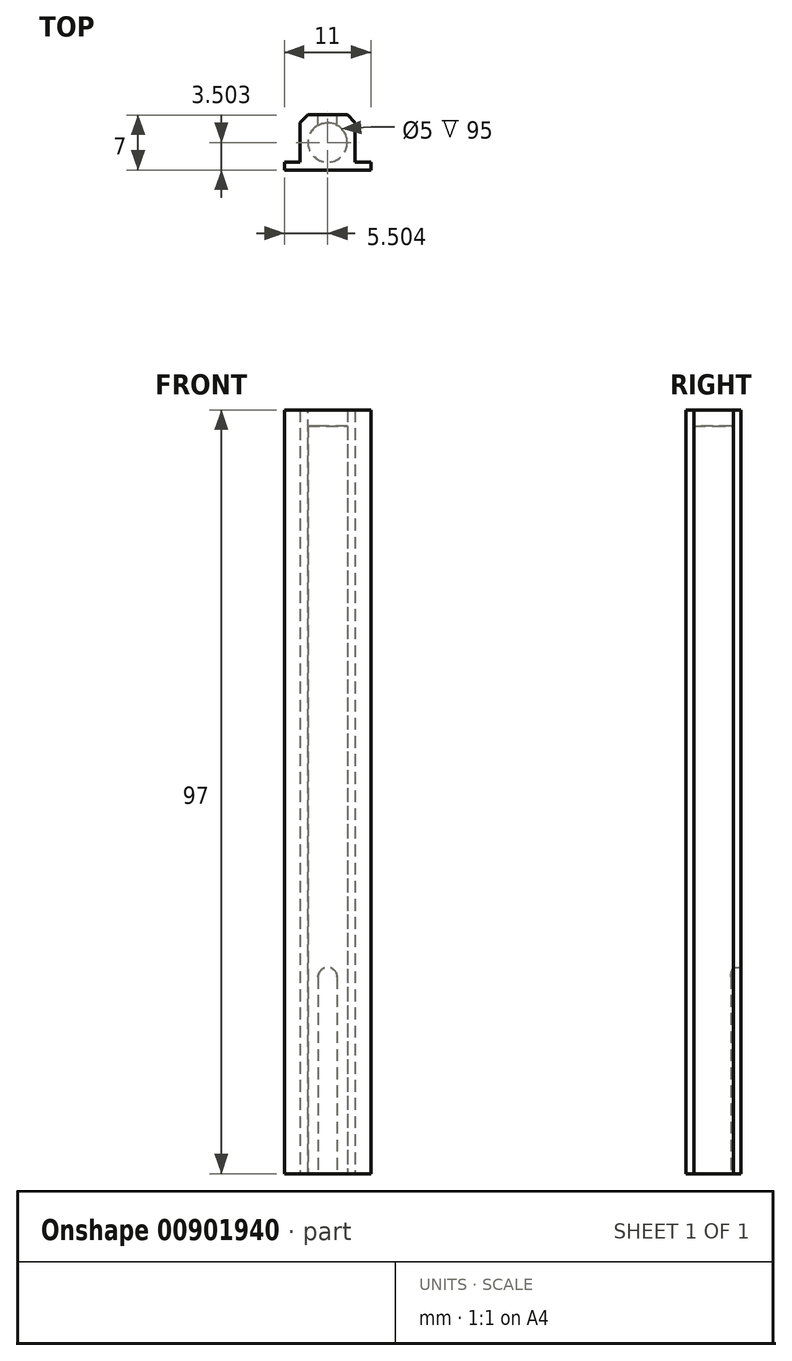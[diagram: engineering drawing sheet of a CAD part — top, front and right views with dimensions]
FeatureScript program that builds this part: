
annotation { "Feature Type Name" : "Feature", "Feature Type Description" : "" }
export const myFeature = defineFeature(function(context is Context, id is Id, definition is map)
    precondition{}
    {
        {
            var Q0;
            Q0=qCreatedBy(makeId("Top.planeOp"),FACE);
            var sketch = newSketch(context, id + "F0", { "sketchPlane" : qUnion([Q0])});
            skLineSegment(sketch, "E0.bottom", {"start": v(-17.39, -38.94) * mm, "end": v(-10.39, -38.94) * mm});
            skLineSegment(sketch, "E0.top", {"start": v(-17.39, -45.94) * mm, "end": v(-10.39, -45.94) * mm});
            skLineSegment(sketch, "E0.left", {"start": v(-17.39, -38.94) * mm, "end": v(-17.39, -45.94) * mm});
            skLineSegment(sketch, "E0.right", {"start": v(-10.39, -38.94) * mm, "end": v(-10.39, -45.94) * mm});
            skLineSegment(sketch, "E1", {"start": v(-17.39, -38.94) * mm, "end": v(-10.39, -45.94) * mm, "construction": true});
            skPoint(sketch, "E2", {"position": v(-17.39, -38.94) * mm});
            skPoint(sketch, "E3", {"position": v(-13.89, -42.44) * mm});
            skLineSegment(sketch, "E4.bottom", {"start": v(-10.39, -45.94) * mm, "end": v(-8.39, -45.94) * mm});
            skLineSegment(sketch, "E4.top", {"start": v(-10.39, -44.94) * mm, "end": v(-8.39, -44.94) * mm});
            skLineSegment(sketch, "E4.left", {"start": v(-10.39, -45.94) * mm, "end": v(-10.39, -44.94) * mm});
            skLineSegment(sketch, "E4.right", {"start": v(-8.39, -45.94) * mm, "end": v(-8.39, -44.94) * mm});
            skLineSegment(sketch, "E5", {"start": v(-13.89, -42.44) * mm, "end": v(-13.89, -45.94) * mm, "construction": true});
            skLineSegment(sketch, "E6.MirrorCS", {"start": v(-17.39, -44.94) * mm, "end": v(-19.39, -44.94) * mm});
            skLineSegment(sketch, "E7.MirrorCS", {"start": v(-17.39, -45.94) * mm, "end": v(-19.39, -45.94) * mm});
            skLineSegment(sketch, "E8.MirrorCS", {"start": v(-19.39, -45.94) * mm, "end": v(-19.39, -44.94) * mm});
            skCircle(sketch, "E9", {"center": v(-13.89, -42.44) * mm, "radius": 2.5 * mm});
            skSolve(sketch);
        }
        {
            var Q0;
            {var subQ2=sQuery(id+"F0.wireOp",EDGE,"E6.MirrorCS");Q0=makeQuery(id+"F0.imprint","IMPRINT",FACE,{"disambiguationData":[TD([[makeQuery(id+"F0.imprint","IMPRINT",EDGE,{"derivedFrom":subQ2}),1.0]])]});}
            var Q1;
            {var subQ3=sQuery(id+"F0.wireOp",EDGE,"E0.bottom");Q1=makeQuery(id+"F0.imprint","IMPRINT",FACE,{"disambiguationData":[TD([[makeQuery(id+"F0.imprint","IMPRINT",EDGE,{"derivedFrom":subQ3}),-1.0]])]});}
            var Q2;
            Q2=makeQuery(id+"F0.imprint","IMPRINT",FACE,{"disambiguationData":[TD([[makeQuery(id+"F0.imprint","IMPRINT",EDGE,{"derivedFrom":sQuery(id+"F0.wireOp",EDGE,"E4.bottom")}),1.0]])]});
            extrude(context, id + "F1", {"entities" : qUnion([Q0, Q1, Q2]), "depth" : 95 * mm, "offsetDistance" : 25 * mm});
        }
        {
            var Q0;
            Q0=makeQuery(id+"F1.opExtrude","CAP_FACE",FACE,{"disambiguationData":[OSD([sQuery(id+"F0.wireOp",EDGE,"E0.bottom"),sQuery(id+"F0.wireOp",EDGE,"E0.top"),sQuery(id+"F0.wireOp",EDGE,"E0.left"),sQuery(id+"F0.wireOp",EDGE,"E0.right"),sQuery(id+"F0.wireOp",EDGE,"E4.bottom"),sQuery(id+"F0.wireOp",EDGE,"E4.top"),sQuery(id+"F0.wireOp",EDGE,"E4.right"),sQuery(id+"F0.wireOp",EDGE,"E6.MirrorCS"),sQuery(id+"F0.wireOp",EDGE,"E7.MirrorCS"),sQuery(id+"F0.wireOp",EDGE,"E8.MirrorCS"),sQuery(id+"F0.wireOp",EDGE,"E9")])],"isStart":false});
            var sketch = newSketch(context, id + "F2", { "sketchPlane" : qUnion([Q0])});
            skLineSegment(sketch, "E10", {"start": v(-19.39, -45.94) * mm, "end": v(-19.39, -44.94) * mm});
            skLineSegment(sketch, "E11", {"start": v(-19.39, -44.94) * mm, "end": v(-17.39, -44.94) * mm});
            skLineSegment(sketch, "E12", {"start": v(-17.39, -44.94) * mm, "end": v(-17.39, -38.94) * mm});
            skLineSegment(sketch, "E13", {"start": v(-17.39, -38.94) * mm, "end": v(-10.39, -38.94) * mm});
            skLineSegment(sketch, "E14", {"start": v(-10.39, -38.94) * mm, "end": v(-10.39, -44.94) * mm});
            skLineSegment(sketch, "E15", {"start": v(-10.39, -44.94) * mm, "end": v(-8.39, -44.94) * mm});
            skLineSegment(sketch, "E16", {"start": v(-8.39, -44.94) * mm, "end": v(-8.39, -45.94) * mm});
            skLineSegment(sketch, "E17", {"start": v(-8.39, -45.94) * mm, "end": v(-19.39, -45.94) * mm});
            skSolve(sketch);
        }
        {
            var Q0;
            Q0 = qSketchRegion(id + "F2", true);
            extrude(context, id + "F3", {"entities" : qUnion([Q0]), "depth" : 2 * mm, "offsetDistance" : 25 * mm});
        }
        {
            var Q0;
            Q0=makeQuery(id+"F1.opExtrude","SWEPT_BODY",BODY,{"disambiguationData":[OSD([sQuery(id+"F0.wireOp",EDGE,"E0.bottom"),sQuery(id+"F0.wireOp",EDGE,"E0.top"),sQuery(id+"F0.wireOp",EDGE,"E0.left"),sQuery(id+"F0.wireOp",EDGE,"E0.right"),sQuery(id+"F0.wireOp",EDGE,"E4.bottom"),sQuery(id+"F0.wireOp",EDGE,"E4.top"),sQuery(id+"F0.wireOp",EDGE,"E4.right"),sQuery(id+"F0.wireOp",EDGE,"E6.MirrorCS"),sQuery(id+"F0.wireOp",EDGE,"E7.MirrorCS"),sQuery(id+"F0.wireOp",EDGE,"E8.MirrorCS"),sQuery(id+"F0.wireOp",EDGE,"E9")])]});
            var Q1;
            Q1=makeQuery(id+"F3.opExtrude","SWEPT_BODY",BODY,{"disambiguationData":[OSD([sQuery(id+"F2.wireOp",EDGE,"E10"),sQuery(id+"F2.wireOp",EDGE,"E11"),sQuery(id+"F2.wireOp",EDGE,"E12"),sQuery(id+"F2.wireOp",EDGE,"E13"),sQuery(id+"F2.wireOp",EDGE,"E14"),sQuery(id+"F2.wireOp",EDGE,"E15"),sQuery(id+"F2.wireOp",EDGE,"E16"),sQuery(id+"F2.wireOp",EDGE,"E17")])]});
            booleanBodies(context, id + "F4", {"operationType" : BooleanOperationType.UNION, "tools" : qUnion([Q0, Q1])});
        }
        {
            var Q0;
            Q0=makeQuery(id+"F4.opBoolean","MERGE",EDGE,{"derivedFrom":[makeQuery(id+"F1.opExtrude","SWEPT_EDGE",EDGE,{"disambiguationData":[OSD([sQuery(id+"F0.wireOp",EDGE,"E0.bottom"),sQuery(id+"F0.wireOp",EDGE,"E0.right")])]}),makeQuery(id+"F3.opExtrude","SWEPT_EDGE",EDGE,{"disambiguationData":[OSD([sQuery(id+"F2.wireOp",EDGE,"E13"),sQuery(id+"F2.wireOp",EDGE,"E14")])]})]});
            chamfer(context, id + "F5", {"entities" : qUnion([Q0]), "width" : 1 * mm, "tangentPropagation" : true});
        }
        {
            var Q0;
            Q0=makeQuery(id+"F4.opBoolean","MERGE",EDGE,{"derivedFrom":[makeQuery(id+"F1.opExtrude","SWEPT_EDGE",EDGE,{"disambiguationData":[OSD([sQuery(id+"F0.wireOp",EDGE,"E0.bottom"),sQuery(id+"F0.wireOp",EDGE,"E0.left")])]}),makeQuery(id+"F3.opExtrude","SWEPT_EDGE",EDGE,{"disambiguationData":[OSD([sQuery(id+"F2.wireOp",EDGE,"E12"),sQuery(id+"F2.wireOp",EDGE,"E13")])]})]});
            chamfer(context, id + "F6", {"entities" : qUnion([Q0]), "width" : 1 * mm, "tangentPropagation" : true});
        }
        {
            var Q0;
            Q0=makeQuery(id+"F4.opBoolean","MERGE",FACE,{"derivedFrom":[makeQuery(id+"F1.opExtrude","SWEPT_FACE",FACE,{"disambiguationData":[OSD([sQuery(id+"F0.wireOp",EDGE,"E0.bottom")])]}),makeQuery(id+"F3.opExtrude","SWEPT_FACE",FACE,{"disambiguationData":[OSD([sQuery(id+"F2.wireOp",EDGE,"E13")])]})]});
            var sketch = newSketch(context, id + "F7", { "sketchPlane" : qUnion([Q0])});
            skLineSegment(sketch, "E18", {"start": v(13.89, 0) * mm, "end": v(13.89, 10.9) * mm, "construction": true});
            skLineSegment(sketch, "E19", {"start": v(13.89, 10.9) * mm, "end": v(13.89, 30.84) * mm, "construction": true});
            skPoint(sketch, "E19.endSnap0", {"position": v(13.89, 5.45) * mm});
            skLineSegment(sketch, "E20.bottom", {"start": v(12.69, 0) * mm, "end": v(15.09, 0) * mm});
            skLineSegment(sketch, "E20.top", {"start": v(12.69, 25) * mm, "end": v(15.09, 25) * mm});
            skLineSegment(sketch, "E20.left", {"start": v(12.69, 0) * mm, "end": v(12.69, 25) * mm});
            skLineSegment(sketch, "E20.right", {"start": v(15.09, 0) * mm, "end": v(15.09, 25) * mm});
            skPoint(sketch, "E21", {"position": v(13.89, 25) * mm});
            skArc(sketch, "E22", {"start": v(15.09, 25) * mm, "mid": v(13.89, 26.2) * mm, "end": v(12.69, 25) * mm});
            skSolve(sketch);
        }
        {
            var Q0;
            Q0=makeQuery(id+"F7.imprint","IMPRINT",FACE,{"disambiguationData":[TD([[makeQuery(id+"F7.imprint","IMPRINT",EDGE,{"derivedFrom":sQuery(id+"F7.wireOp",EDGE,"E20.bottom")}),-1.0]])]});
            var Q1;
            Q1=makeQuery(id+"F7.imprint","IMPRINT",FACE,{"disambiguationData":[TD([[makeQuery(id+"F7.imprint","IMPRINT",EDGE,{"derivedFrom":sQuery(id+"F7.wireOp",EDGE,"E20.top")}),1.0]])]});
            extrude(context, id + "F8", {"entities" : qUnion([Q0, Q1]), "operationType" : NewBodyOperationType.REMOVE, "endBound" : BoundingType.UP_TO_NEXT, "oppositeDirection" : true, "depth" : 25 * mm, "offsetDistance" : 25 * mm});
        }
    });
